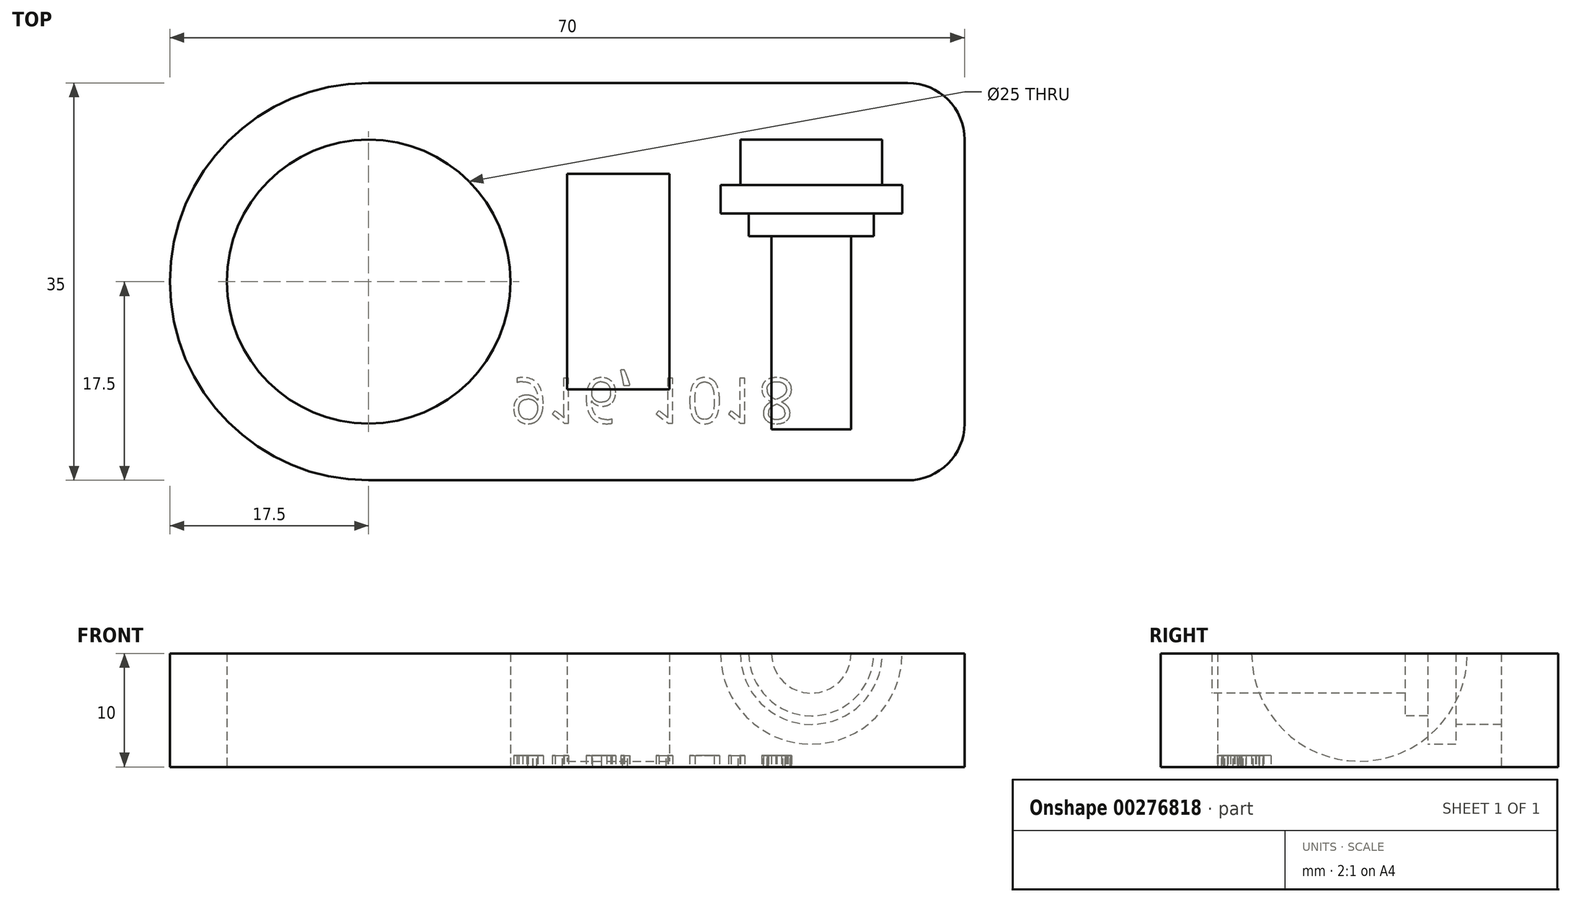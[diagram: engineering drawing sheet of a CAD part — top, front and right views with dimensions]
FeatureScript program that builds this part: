
annotation { "Feature Type Name" : "Feature", "Feature Type Description" : "" }
export const myFeature = defineFeature(function(context is Context, id is Id, definition is map)
    precondition{}
    {
        {
            var Q0;
            Q0=qCreatedBy(makeId("Top.planeOp"),FACE);
            var sketch = newSketch(context, id + "F0", { "sketchPlane" : qUnion([Q0])});
            skLineSegment(sketch, "E0.bottom", {"start": v(17.5, 0) * mm, "end": v(65, 0) * mm});
            skLineSegment(sketch, "E0.top", {"start": v(17.5, 35) * mm, "end": v(65, 35) * mm});
            skLineSegment(sketch, "E0.left", {"start": v(0, 17.5) * mm, "end": v(0, 17.5) * mm});
            skLineSegment(sketch, "E0.right", {"start": v(70, 5) * mm, "end": v(70, 30) * mm});
            skLineSegment(sketch, "E1.bottom", {"start": v(0, 0) * mm, "end": v(17.5, 0) * mm, "construction": true});
            skLineSegment(sketch, "E1.top", {"start": v(0, 17.5) * mm, "end": v(17.5, 17.5) * mm, "construction": true});
            skLineSegment(sketch, "E1.left", {"start": v(0, 0) * mm, "end": v(0, 17.5) * mm, "construction": true});
            skLineSegment(sketch, "E1.right", {"start": v(17.5, 0) * mm, "end": v(17.5, 17.5) * mm, "construction": true});
            skCircle(sketch, "E2", {"center": v(17.5, 17.5) * mm, "radius": 12.5 * mm});
            skPoint(sketch, "E3.visualSharp", {"position": v(0, 0) * mm});
            skArc(sketch, "E3.filletArc", {"start": v(0, 17.5) * mm, "mid": v(5.13, 5.13) * mm, "end": v(17.5, 0) * mm});
            skPoint(sketch, "E4.visualSharp", {"position": v(0, 35) * mm});
            skArc(sketch, "E4.filletArc", {"start": v(17.5, 35) * mm, "mid": v(5.13, 29.87) * mm, "end": v(0, 17.5) * mm});
            skPoint(sketch, "E5.visualSharp", {"position": v(70, 35) * mm});
            skArc(sketch, "E5.filletArc", {"start": v(70, 30) * mm, "mid": v(68.54, 33.54) * mm, "end": v(65, 35) * mm});
            skPoint(sketch, "E6.visualSharp", {"position": v(70, 0) * mm});
            skArc(sketch, "E6.filletArc", {"start": v(65, 0) * mm, "mid": v(68.54, 1.46) * mm, "end": v(70, 5) * mm});
            skSolve(sketch);
        }
        {
            var Q0;
            Q0=makeQuery(id+"F0.imprint","IMPRINT",FACE,{"disambiguationData":[TD([[makeQuery(id+"F0.imprint","IMPRINT",EDGE,{"derivedFrom":sQuery(id+"F0.wireOp",EDGE,"E0.bottom")}),1.0]])]});
            extrude(context, id + "F1", {"entities" : qUnion([Q0]), "depth" : 10 * mm});
        }
        {
            var Q0;
            Q0=makeQuery(id+"F1.opExtrude","CAP_FACE",FACE,{"disambiguationData":[OSD([sQuery(id+"F0.wireOp",EDGE,"E0.bottom"),sQuery(id+"F0.wireOp",EDGE,"E0.top"),sQuery(id+"F0.wireOp",EDGE,"E0.right"),sQuery(id+"F0.wireOp",EDGE,"E2"),sQuery(id+"F0.wireOp",EDGE,"E3.filletArc"),sQuery(id+"F0.wireOp",EDGE,"E4.filletArc"),sQuery(id+"F0.wireOp",EDGE,"E5.filletArc"),sQuery(id+"F0.wireOp",EDGE,"E6.filletArc")])],"isStart":false});
            var sketch = newSketch(context, id + "F2", { "sketchPlane" : qUnion([Q0])});
            skLineSegment(sketch, "E7.bottom", {"start": v(0, 0) * mm, "end": v(35, 0) * mm, "construction": true});
            skLineSegment(sketch, "E7.top", {"start": v(0, 17.5) * mm, "end": v(35, 17.5) * mm, "construction": true});
            skLineSegment(sketch, "E7.left", {"start": v(0, 0) * mm, "end": v(0, 17.5) * mm, "construction": true});
            skLineSegment(sketch, "E7.right", {"start": v(35, 0) * mm, "end": v(35, 17.5) * mm, "construction": true});
            skLineSegment(sketch, "E8.bottom", {"start": v(35, 17.5) * mm, "end": v(44, 17.5) * mm});
            skLineSegment(sketch, "E8.top", {"start": v(35, 8) * mm, "end": v(44, 8) * mm});
            skLineSegment(sketch, "E8.left", {"start": v(35, 17.5) * mm, "end": v(35, 8) * mm});
            skLineSegment(sketch, "E8.right", {"start": v(44, 17.5) * mm, "end": v(44, 8) * mm});
            skLineSegment(sketch, "E9.bottom", {"start": v(0, 0) * mm, "end": v(56.5, 0) * mm, "construction": true});
            skLineSegment(sketch, "E9.top", {"start": v(0, 30) * mm, "end": v(56.5, 30) * mm, "construction": true});
            skLineSegment(sketch, "E9.left", {"start": v(0, 0) * mm, "end": v(0, 30) * mm, "construction": true});
            skLineSegment(sketch, "E9.right", {"start": v(56.5, 0) * mm, "end": v(56.5, 30) * mm, "construction": true});
            skLineSegment(sketch, "E10.bottom", {"start": v(56.5, 30) * mm, "end": v(62.75, 30) * mm});
            skLineSegment(sketch, "E10.left", {"start": v(56.5, 30) * mm, "end": v(56.5, 26) * mm});
            skLineSegment(sketch, "E10.right", {"start": v(62.75, 30) * mm, "end": v(62.75, 26) * mm});
            skLineSegment(sketch, "E11.bottom", {"start": v(62.75, 26) * mm, "end": v(64.5, 26) * mm});
            skLineSegment(sketch, "E11.top", {"start": v(62, 23.5) * mm, "end": v(64.5, 23.5) * mm});
            skLineSegment(sketch, "E11.left", {"start": v(56.5, 26) * mm, "end": v(56.5, 23.5) * mm});
            skLineSegment(sketch, "E11.right", {"start": v(64.5, 26) * mm, "end": v(64.5, 23.5) * mm});
            skLineSegment(sketch, "E12.top", {"start": v(60, 21.5) * mm, "end": v(62, 21.5) * mm});
            skLineSegment(sketch, "E12.left", {"start": v(56.5, 23.5) * mm, "end": v(56.5, 21.5) * mm});
            skLineSegment(sketch, "E12.right", {"start": v(62, 23.5) * mm, "end": v(62, 21.5) * mm});
            skLineSegment(sketch, "E13.top", {"start": v(56.5, 4.5) * mm, "end": v(60, 4.5) * mm});
            skLineSegment(sketch, "E13.left", {"start": v(56.5, 21.5) * mm, "end": v(56.5, 4.5) * mm});
            skLineSegment(sketch, "E13.right", {"start": v(60, 21.5) * mm, "end": v(60, 4.5) * mm});
            skSolve(sketch);
        }
        {
            var Q0;
            Q0=makeQuery(id+"F2.imprint","IMPRINT",FACE,{"disambiguationData":[TD([[makeQuery(id+"F2.imprint","IMPRINT",EDGE,{"derivedFrom":sQuery(id+"F2.wireOp",EDGE,"E8.bottom")}),-1.0]])]});
            var Q1;
            Q1=sQuery(id+"F2.wireOp",EDGE,"E8.bottom");
            revolve(context, id + "F3", {"operationType" : NewBodyOperationType.REMOVE, "entities" : qUnion([Q0]), "axis" : qUnion([Q1]), "revolveType" : RevolveType.FULL, "oppositeDirection" : true});
        }
        {
            var Q0;
            Q0=makeQuery(id+"F2.imprint","IMPRINT",FACE,{"disambiguationData":[TD([[makeQuery(id+"F2.imprint","IMPRINT",EDGE,{"derivedFrom":sQuery(id+"F2.wireOp",EDGE,"E10.bottom")}),-1.0]])]});
            var Q1;
            Q1=sQuery(id+"F2.wireOp",EDGE,"E13.left");
            revolve(context, id + "F4", {"operationType" : NewBodyOperationType.REMOVE, "entities" : qUnion([Q0]), "axis" : qUnion([Q1]), "revolveType" : RevolveType.FULL, "oppositeDirection" : true});
        }
        {
            var Q0;
            Q0=makeQuery(id+"F1.opExtrude","CAP_FACE",FACE,{"disambiguationData":[OSD([sQuery(id+"F0.wireOp",EDGE,"E0.bottom"),sQuery(id+"F0.wireOp",EDGE,"E0.top"),sQuery(id+"F0.wireOp",EDGE,"E0.right"),sQuery(id+"F0.wireOp",EDGE,"E2"),sQuery(id+"F0.wireOp",EDGE,"E3.filletArc"),sQuery(id+"F0.wireOp",EDGE,"E4.filletArc"),sQuery(id+"F0.wireOp",EDGE,"E5.filletArc"),sQuery(id+"F0.wireOp",EDGE,"E6.filletArc")])],"isStart":true});
            var sketch = newSketch(context, id + "F5", { "sketchPlane" : qUnion([Q0])});
            skLineSegment(sketch, "E14.bottom", {"start": v(0, 0) * mm, "end": v(30, 0) * mm, "construction": true});
            skLineSegment(sketch, "E14.top", {"start": v(0, -5) * mm, "end": v(30, -5) * mm, "construction": true});
            skLineSegment(sketch, "E14.left", {"start": v(0, 0) * mm, "end": v(0, -5) * mm, "construction": true});
            skLineSegment(sketch, "E14.right", {"start": v(30, 0) * mm, "end": v(30, -5) * mm, "construction": true});
            skText(sketch, "E15", { "text": "916, 1018", "fontName": "OpenSans-Regular.ttf"});
            const initialGuessF5  = {"E15": [0.03, -0.009, 1, 0, 0.004]};
            skSetInitialGuess(sketch, initialGuessF5);
            skSolve(sketch);
        }
        {
            var Q0;
            Q0 = qSketchRegion(id + "F5", true);
            extrude(context, id + "F6", {"entities" : qUnion([Q0]), "operationType" : NewBodyOperationType.REMOVE, "oppositeDirection" : true, "depth" : 1 * mm});
        }
    });
